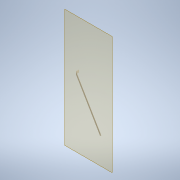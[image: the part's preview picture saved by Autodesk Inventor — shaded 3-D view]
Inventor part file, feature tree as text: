
AUTODESK INVENTOR PART (.ipt)
format: ipt  version: 2021 (Build 250183000, 183)  size: 160,768 bytes
history: native  units: mm
features: extrude x6, sketch x6, fillet x2, other x2, plane x1
ambient origin geometry x8: Origin, YZ Plane, XZ Plane, XY Plane, X Axis, Y Axis, Z Axis, Center Point
bodies: Solid1 (feature_tree)
feature tree (17):
  plane  "Work Plane1"
  extrude  "Extrusion1"  Depth=30.0mm
  extrude  "Extrusion2"  Depth=26.110126mm
  extrude  "Extrusion3"  Depth=6.0mm TaperAngle=0.0deg
  fillet  "Fillet1"  Radius=3.0mm
  extrude  "Extrusion4"  Depth=60.0mm TaperAngle=0.0deg
  fillet  "Fillet2"  Radius=6.0mm
  extrude  "Extrusion5"  Depth=2.0mm
  extrude  "Extrusion6"  Depth=10.0mm
  sketch  "Sketch1"  dims[d0=30.0mm d2=180.0mm]
  sketch  "Sketch2"  dims[d3=1350.0mm d4=26.110126mm]
  sketch  "Sketch3"  dims[d5=1060.0mm d6=6.0mm d7=0.0mm d8=3.0mm d9=0.0mm]
  sketch  "Sketch4"  dims[d10=3.0mm d11=60.0mm d12=0.0mm d13=6.0mm]
  sketch  "Sketch5"  dims[d14=90.0mm d15=45.0mm d16=0.0mm d17=0.0mm d18=2.0mm]
  sketch  "Sketch6"  dims[d19=51.8mm d20=32.2mm d21=10.0mm d22=10.0mm d23=0.0mm d24=10.0mm d25=15.0mm d26=27.5mm d27=10.0mm d28=0.0mm]
  other  "cover_final_assembly.iam"
  other  "wheelchair_box_extended:1"
